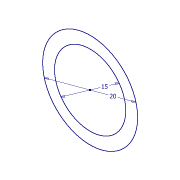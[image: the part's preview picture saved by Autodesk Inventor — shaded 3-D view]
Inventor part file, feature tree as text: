
AUTODESK INVENTOR PART (.ipt)
format: ipt  version: 2020 (Build 240168000, 168)  size: 86,528 bytes
history: native  units: mm
features: extrude x2, sketch x2, chamfer x1
ambient origin geometry x8: Origin, YZ Plane, XZ Plane, XY Plane, X Axis, Y Axis, Z Axis, Center Point
bodies: Volumenkörper1 (feature_tree)
feature tree (5):
  extrude  "Extrusion1"  Depth=20.0mm
  extrude  "Extrusion2"  Depth=5.0mm TaperAngle=0.0deg
  chamfer  "Fase1"  Distance=2.0mm Angle=45.0deg
  sketch  "Skizze1"  dims[d0=15.0mm d1=20.0mm]
  sketch  "Skizze2"  dims[d2=100.0mm d3=0.0mm d4=5.0mm d5=0.0mm d6=2.0mm d7=2.0mm d8=45.0deg]
